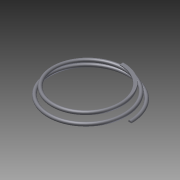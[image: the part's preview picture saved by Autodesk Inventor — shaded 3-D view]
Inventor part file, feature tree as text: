
AUTODESK INVENTOR PART (.ipt)
format: ipt  version: 2011 (Build 150239000, 239)  size: 223,232 bytes
history: native  units: mm (DEFAULTED — no unit token found)
features: sketch x3, extrude x2, helix x1, plane x1
ambient origin geometry x8: Origin, YZ Plane, XZ Plane, XY Plane, X Axis, Y Axis, Z Axis, Center Point
bodies: Solid1 (feature_tree)
feature tree (7):
  helix  "Coil1"  [1 undecoded]
  plane  "Work Plane1"
  extrude  "Extrusion1"  Depth=24.4348mm
  extrude  "Extrusion2"  Depth=3.2512mm
  sketch  "Sketch1"  dims[d4=20.0mm d5=-5.235988mm d6=45.0deg d7=45.0deg d8=0.0mm d9=0.0mm d10=3.2512mm d11=24.4348mm]
  sketch  "Sketch2"  dims[d12=24.4348mm d13=3.2512mm]
  sketch  "Sketch3"  dims[d14=0.0mm d15=24.4348mm d16=24.4348mm d17=3.2512mm d18=0.0mm]
note: 1 required parameter value undecoded (feature->parameter linkage not recoverable at this tier; creation-order binding heuristic only, values carry confidence <= 0.55)
